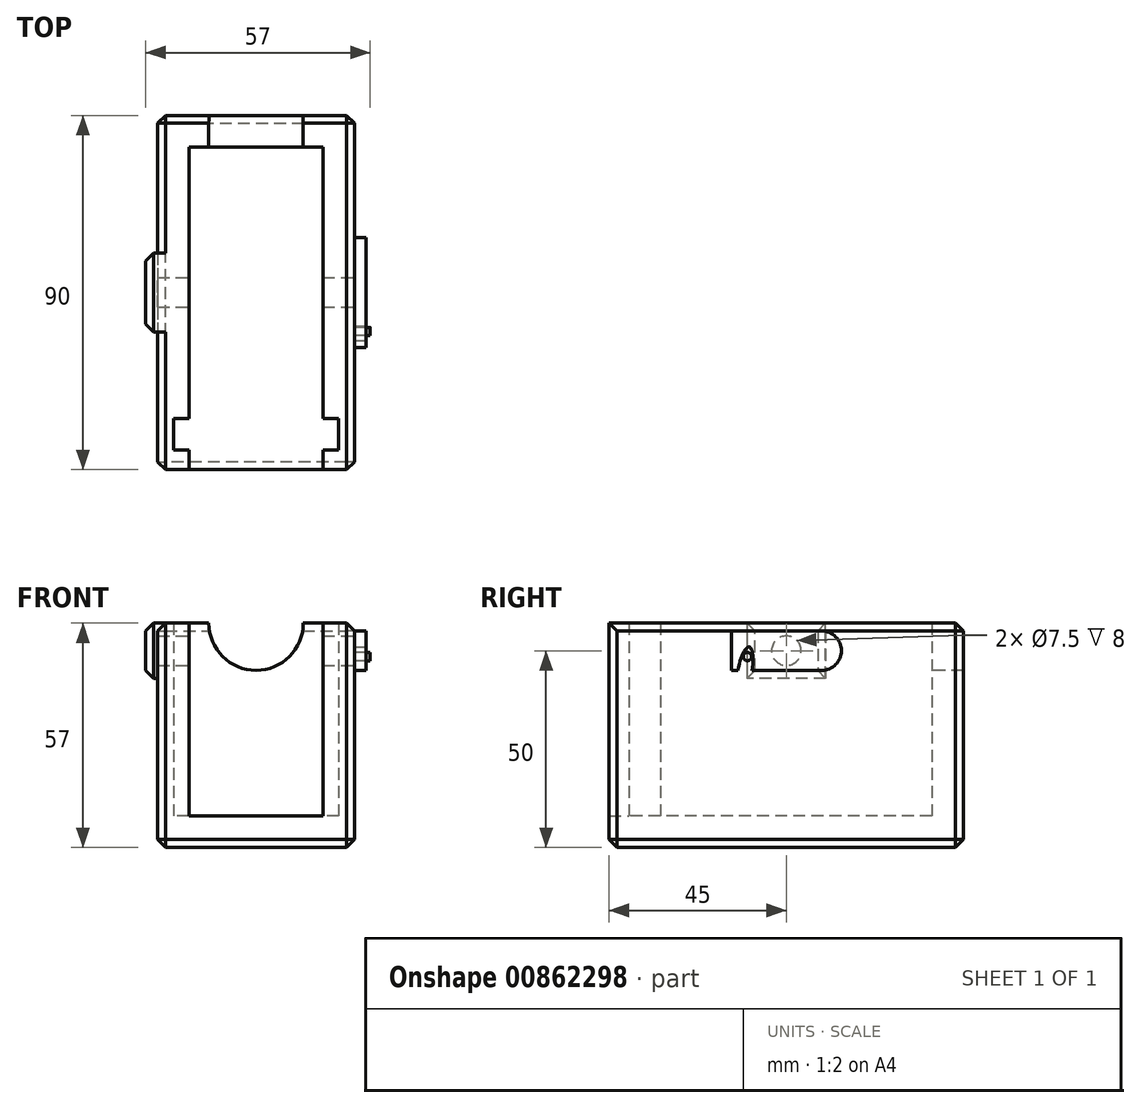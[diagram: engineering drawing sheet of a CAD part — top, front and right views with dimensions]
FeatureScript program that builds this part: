
annotation { "Feature Type Name" : "Feature", "Feature Type Description" : "" }
export const myFeature = defineFeature(function(context is Context, id is Id, definition is map)
    precondition{}
    {
        {
            var Q0;
            Q0=qCreatedBy(makeId("Top.planeOp"),FACE);
            var sketch = newSketch(context, id + "F0", { "sketchPlane" : qUnion([Q0])});
            skLineSegment(sketch, "E0.bottom", {"start": v(25, 45) * mm, "end": v(-25, 45) * mm});
            skLineSegment(sketch, "E0.top", {"start": v(25, -45) * mm, "end": v(-25, -45) * mm});
            skLineSegment(sketch, "E0.left", {"start": v(25, 45) * mm, "end": v(25, -45) * mm});
            skLineSegment(sketch, "E0.right", {"start": v(-25, 45) * mm, "end": v(-25, -45) * mm});
            skPoint(sketch, "E0.middle", {"position": v(0, 0) * mm});
            skSolve(sketch);
        }
        {
            var Q0;
            Q0 = qSketchRegion(id + "F0", true);
            extrude(context, id + "F1", {"entities" : qUnion([Q0]), "depth" : -8 * mm, "offsetDistance" : 25 * mm});
        }
        {
            var Q0;
            Q0=qCreatedBy(makeId("Top.planeOp"),FACE);
            var sketch = newSketch(context, id + "F2", { "sketchPlane" : qUnion([Q0])});
            skLineSegment(sketch, "E1.bottom", {"start": v(-25, 45) * mm, "end": v(25, 45) * mm, "construction": true});
            skLineSegment(sketch, "E1.top", {"start": v(-25, -45) * mm, "end": v(25, -45) * mm, "construction": true});
            skLineSegment(sketch, "E1.left", {"start": v(-25, 45) * mm, "end": v(-25, -45) * mm, "construction": true});
            skLineSegment(sketch, "E1.right", {"start": v(25, 45) * mm, "end": v(25, -45) * mm, "construction": true});
            skPoint(sketch, "E1.middle", {"position": v(0, 0) * mm});
            skLineSegment(sketch, "E2.bottom", {"start": v(-25, 45) * mm, "end": v(25, 45) * mm});
            skLineSegment(sketch, "E2.left", {"start": v(-25, 45) * mm, "end": v(-25, 37) * mm});
            skLineSegment(sketch, "E2.right", {"start": v(25, 45) * mm, "end": v(25, 37) * mm});
            skLineSegment(sketch, "E3.bottom", {"start": v(-25, 45) * mm, "end": v(-17, 45) * mm});
            skLineSegment(sketch, "E3.top", {"start": v(-25, -45) * mm, "end": v(-17, -45) * mm});
            skLineSegment(sketch, "E3.left", {"start": v(-25, 45) * mm, "end": v(-25, -45) * mm});
            skLineSegment(sketch, "E4", {"start": v(17, 37) * mm, "end": v(-17, 37) * mm});
            skLineSegment(sketch, "E5.bottom", {"start": v(25, 45) * mm, "end": v(17, 45) * mm});
            skLineSegment(sketch, "E5.top", {"start": v(25, -45) * mm, "end": v(17, -45) * mm});
            skLineSegment(sketch, "E5.left", {"start": v(25, 45) * mm, "end": v(25, -45) * mm});
            skLineSegment(sketch, "E6", {"start": v(-17, 45) * mm, "end": v(-17, 37) * mm, "construction": true});
            skLineSegment(sketch, "E7", {"start": v(-25, 37) * mm, "end": v(-17, 37) * mm, "construction": true});
            skLineSegment(sketch, "E8", {"start": v(17, 45) * mm, "end": v(17, 37) * mm, "construction": true});
            skLineSegment(sketch, "E9", {"start": v(17, 37) * mm, "end": v(25, 37) * mm, "construction": true});
            skLineSegment(sketch, "E10", {"start": v(-17, 37) * mm, "end": v(-17, -32) * mm});
            skLineSegment(sketch, "E11", {"start": v(17, 37) * mm, "end": v(17, -32) * mm});
            skLineSegment(sketch, "E12", {"start": v(17, -45) * mm, "end": v(17, -40) * mm});
            skLineSegment(sketch, "E13", {"start": v(-17, -45) * mm, "end": v(-17, -40) * mm});
            skLineSegment(sketch, "E14", {"start": v(-17, -32) * mm, "end": v(-21, -32) * mm});
            skLineSegment(sketch, "E15", {"start": v(-21, -32) * mm, "end": v(-21, -40) * mm});
            skLineSegment(sketch, "E16", {"start": v(-21, -40) * mm, "end": v(-17, -40) * mm});
            skLineSegment(sketch, "E17", {"start": v(17, -32) * mm, "end": v(21, -32) * mm});
            skLineSegment(sketch, "E18", {"start": v(21, -32) * mm, "end": v(21, -40) * mm});
            skLineSegment(sketch, "E19", {"start": v(21, -40) * mm, "end": v(17, -40) * mm});
            skSolve(sketch);
        }
        {
            var Q0;
            Q0 = qSketchRegion(id + "F2", true);
            extrude(context, id + "F3", {"entities" : qUnion([Q0]), "operationType" : NewBodyOperationType.ADD, "depth" : 49 * mm, "offsetDistance" : 25 * mm});
        }
        {
            var Q0;
            Q0=qCreatedBy(makeId("Right.planeOp"),FACE);
            var sketch = newSketch(context, id + "F4", { "sketchPlane" : qUnion([Q0])});
            skLineSegment(sketch, "E20", {"start": v(0, 0) * mm, "end": v(0, 42) * mm, "construction": true});
            skCircle(sketch, "E21", {"center": v(0, 42) * mm, "radius": 3.75 * mm});
            skSolve(sketch);
        }
        {
            var Q0;
            Q0 = qSketchRegion(id + "F4", true);
            extrude(context, id + "F5", {"entities" : qUnion([Q0]), "operationType" : NewBodyOperationType.REMOVE, "endBound" : BoundingType.SYMMETRIC, "oppositeDirection" : true, "depth" : 50 * mm, "offsetDistance" : 25 * mm});
        }
        {
            var Q0;
            Q0=qCreatedBy(makeId("Front.planeOp"),FACE);
            var sketch = newSketch(context, id + "F6", { "sketchPlane" : qUnion([Q0])});
            skLineSegment(sketch, "E22", {"start": v(0, 0) * mm, "end": v(0, 49) * mm, "construction": true});
            skArc(sketch, "E23", {"start": v(12, 49) * mm, "mid": v(0, 37) * mm, "end": v(-12, 49) * mm});
            skLineSegment(sketch, "E24", {"start": v(12, 49) * mm, "end": v(-12, 49) * mm});
            skSolve(sketch);
        }
        {
            var Q0;
            Q0 = qSketchRegion(id + "F6", true);
            extrude(context, id + "F7", {"entities" : qUnion([Q0]), "operationType" : NewBodyOperationType.REMOVE, "oppositeDirection" : true, "depth" : 50 * mm, "offsetDistance" : 25 * mm});
        }
        {
            var Q0;
            Q0=qCreatedBy(makeId("Right.planeOp"),FACE);
            var sketch = newSketch(context, id + "F8", { "sketchPlane" : qUnion([Q0])});
            skLineSegment(sketch, "E25", {"start": v(0, 0) * mm, "end": v(0, 42) * mm, "construction": true});
            skLineSegment(sketch, "E26.bottom", {"start": v(10, 49) * mm, "end": v(-10, 49) * mm});
            skLineSegment(sketch, "E26.top", {"start": v(10, 35) * mm, "end": v(-10, 35) * mm});
            skLineSegment(sketch, "E26.left", {"start": v(10, 49) * mm, "end": v(10, 35) * mm});
            skLineSegment(sketch, "E26.right", {"start": v(-10, 49) * mm, "end": v(-10, 35) * mm});
            skPoint(sketch, "E26.middle", {"position": v(0, 42) * mm});
            skSolve(sketch);
        }
        {
            var Q0;
            Q0 = qSketchRegion(id + "F8", true);
            extrude(context, id + "F9", {"entities" : qUnion([Q0]), "operationType" : NewBodyOperationType.ADD, "oppositeDirection" : true, "depth" : 28 * mm, "offsetDistance" : 25 * mm, "hasSecondDirection" : true, "secondDirectionOppositeDirection" : false, "secondDirectionDepth" : -25 * mm});
        }
        {
            var Q0;
            Q0=qCreatedBy(makeId("Right.planeOp"),FACE);
            var sketch = newSketch(context, id + "F10", { "sketchPlane" : qUnion([Q0])});
            skLineSegment(sketch, "E27", {"start": v(0, 0) * mm, "end": v(0, 42) * mm, "construction": true});
            skLineSegment(sketch, "E28.bottom", {"start": v(9, 47) * mm, "end": v(-14, 47) * mm});
            skLineSegment(sketch, "E28.top", {"start": v(9, 37) * mm, "end": v(-8.72, 37) * mm});
            skLineSegment(sketch, "E28.right", {"start": v(-14, 47) * mm, "end": v(-14, 37) * mm});
            skPoint(sketch, "E28.middle", {"position": v(0, 42) * mm});
            skLineSegment(sketch, "E29", {"start": v(-14, 37) * mm, "end": v(-12.27, 37) * mm, "construction": true});
            skArc(sketch, "E30", {"start": v(9, 37) * mm, "mid": v(12.54, 38.46) * mm, "end": v(14, 42) * mm});
            skLineSegment(sketch, "E31", {"start": v(9, 37) * mm, "end": v(9, 47) * mm, "construction": true});
            skArc(sketch, "E32", {"start": v(14, 42) * mm, "mid": v(12.54, 45.54) * mm, "end": v(9, 47) * mm});
            skPoint(sketch, "E33.orphan", {"position": v(14, 37) * mm});
            skPoint(sketch, "E34.orphan", {"position": v(14, 47) * mm});
            skEllipticalArc(sketch, "E35", {});
            skLineSegment(sketch, "E36", {"start": v(9, 37) * mm, "end": v(-8.72, 37) * mm, "construction": true});
            skLineSegment(sketch, "E37", {"start": v(-8.72, 37) * mm, "end": v(9, 37) * mm});
            skLineSegment(sketch, "E38", {"start": v(-12.27, 37) * mm, "end": v(-14, 37) * mm});
            skLineSegment(sketch, "E39.trimOffspring", {"start": v(-8.72, 37) * mm, "end": v(9, 37) * mm, "construction": true});
            skLineSegment(sketch, "E40.trimOffspring", {"start": v(-12.28, 37) * mm, "end": v(-14, 37) * mm});
            const initialGuessF10  = {"E35": [-0.010498499999999997, 0.037, 0.17990183921045588, 0.983684567454779, 0.006, 0.00175, 4.765680137042853, 1.6240874834530625]};
            skSetInitialGuess(sketch, initialGuessF10);
            skSolve(sketch);
        }
        {
            var Q0;
            Q0 = qSketchRegion(id + "F10", true);
            extrude(context, id + "F11", {"entities" : qUnion([Q0]), "operationType" : NewBodyOperationType.ADD, "depth" : 28 * mm, "offsetDistance" : 25 * mm, "hasSecondDirection" : true, "secondDirectionOppositeDirection" : true, "secondDirectionDepth" : -25 * mm});
        }
        {
            var Q0;
            Q0=qCreatedBy(makeId("Right.planeOp"),FACE);
            var sketch = newSketch(context, id + "F12", { "sketchPlane" : qUnion([Q0])});
            skCircle(sketch, "E41", {"center": v(-9.9, 40.5) * mm, "radius": 1.05 * mm});
            skSolve(sketch);
        }
        {
            var Q0;
            Q0 = qSketchRegion(id + "F12", true);
            extrude(context, id + "F13", {"entities" : qUnion([Q0]), "operationType" : NewBodyOperationType.ADD, "depth" : 29 * mm, "offsetDistance" : 25 * mm, "hasSecondDirection" : true, "secondDirectionOppositeDirection" : false, "secondDirectionDepth" : 25 * mm});
        }
        {
            var Q0;
            Q0=makeQuery(id+"F1.opExtrude","CAP_EDGE",EDGE,{"disambiguationData":[OSD([sQuery(id+"F0.wireOp",EDGE,"E0.left")])],"isStart":false});
            var Q1;
            Q1=makeQuery(id+"F3.boolean.opBoolean","MERGE",EDGE,{"derivedFrom":[makeQuery(id+"F1.opExtrude","SWEPT_EDGE",EDGE,{"disambiguationData":[OSD([sQuery(id+"F0.wireOp",EDGE,"E0.top"),sQuery(id+"F0.wireOp",EDGE,"E0.left")])]}),makeQuery(id+"F3.opExtrude","SWEPT_EDGE",EDGE,{"disambiguationData":[OSD([sQuery(id+"F2.wireOp",EDGE,"E5.top"),sQuery(id+"F2.wireOp",EDGE,"E5.left")])]})]});
            var Q2;
            Q2=makeQuery(id+"F1.opExtrude","CAP_EDGE",EDGE,{"disambiguationData":[OSD([sQuery(id+"F0.wireOp",EDGE,"E0.top")])],"isStart":false});
            var Q3;
            Q3=makeQuery(id+"F3.boolean.opBoolean","MERGE",EDGE,{"derivedFrom":[makeQuery(id+"F1.opExtrude","SWEPT_EDGE",EDGE,{"disambiguationData":[OSD([sQuery(id+"F0.wireOp",EDGE,"E0.top"),sQuery(id+"F0.wireOp",EDGE,"E0.right")])]}),makeQuery(id+"F3.opExtrude","SWEPT_EDGE",EDGE,{"disambiguationData":[OSD([sQuery(id+"F2.wireOp",EDGE,"E3.top"),sQuery(id+"F2.wireOp",EDGE,"E3.left")])]})]});
            var Q4;
            Q4=makeQuery(id+"F1.opExtrude","CAP_EDGE",EDGE,{"disambiguationData":[OSD([sQuery(id+"F0.wireOp",EDGE,"E0.right")])],"isStart":false});
            var Q5;
            Q5=makeQuery(id+"F3.boolean.opBoolean","MERGE",EDGE,{"derivedFrom":[makeQuery(id+"F1.opExtrude","SWEPT_EDGE",EDGE,{"disambiguationData":[OSD([sQuery(id+"F0.wireOp",EDGE,"E0.bottom"),sQuery(id+"F0.wireOp",EDGE,"E0.right")])]}),makeQuery(id+"F3.opExtrude","SWEPT_EDGE",EDGE,{"disambiguationData":[OSD([sQuery(id+"F2.wireOp",EDGE,"E3.bottom"),sQuery(id+"F2.wireOp",EDGE,"E3.left")])]})]});
            var Q6;
            Q6=makeQuery(id+"F3.boolean.opBoolean","MERGE",EDGE,{"derivedFrom":[makeQuery(id+"F1.opExtrude","SWEPT_EDGE",EDGE,{"disambiguationData":[OSD([sQuery(id+"F0.wireOp",EDGE,"E0.bottom"),sQuery(id+"F0.wireOp",EDGE,"E0.left")])]}),makeQuery(id+"F3.opExtrude","SWEPT_EDGE",EDGE,{"disambiguationData":[OSD([sQuery(id+"F2.wireOp",EDGE,"E5.bottom"),sQuery(id+"F2.wireOp",EDGE,"E5.left")])]})]});
            var Q7;
            Q7=makeQuery(id+"F1.opExtrude","CAP_EDGE",EDGE,{"disambiguationData":[OSD([sQuery(id+"F0.wireOp",EDGE,"E0.bottom")])],"isStart":false});
            var Q8;
            Q8=makeQuery(id+"F9.opExtrude","CAP_EDGE",EDGE,{"disambiguationData":[OSD([sQuery(id+"F8.wireOp",EDGE,"E26.bottom")])],"isStart":false});
            var Q9;
            {var subQ0=sQuery(id+"F2.wireOp",EDGE,"E5.bottom");var subQ2=sQuery(id+"F2.wireOp",EDGE,"E3.bottom");var subQ3=sQuery(id+"F2.wireOp",EDGE,"E2.bottom");Q9=makeQuery(id+"F7.boolean.opBoolean","SPLIT",EDGE,{"disambiguationData":[TD([makeQuery(id+"F1.opExtrude","SWEPT_FACE",FACE,{"disambiguationData":[OSD([sQuery(id+"F0.wireOp",EDGE,"E0.right")])]})])],"derivedFrom":makeQuery(id+"F3.opExtrude","CAP_EDGE",EDGE,{"disambiguationData":[OSD([subQ3,subQ2,subQ0])],"isStart":false})});}
            var Q10;
            {var subQ1=sQuery(id+"F2.wireOp",EDGE,"E5.bottom");var subQ2=sQuery(id+"F2.wireOp",EDGE,"E3.bottom");var subQ3=sQuery(id+"F2.wireOp",EDGE,"E2.bottom");Q10=makeQuery(id+"F7.boolean.opBoolean","SPLIT",EDGE,{"disambiguationData":[TD([makeQuery(id+"F1.opExtrude","SWEPT_FACE",FACE,{"disambiguationData":[OSD([sQuery(id+"F0.wireOp",EDGE,"E0.left")])]})])],"derivedFrom":makeQuery(id+"F3.opExtrude","CAP_EDGE",EDGE,{"disambiguationData":[OSD([subQ3,subQ2,subQ1])],"isStart":false})});}
            var Q11;
            Q11=makeQuery(id+"F3.opExtrude","CAP_EDGE",EDGE,{"disambiguationData":[OSD([sQuery(id+"F2.wireOp",EDGE,"E5.left")])],"isStart":false});
            var Q12;
            {var subQ1=sQuery(id+"F2.wireOp",EDGE,"E3.left");Q12=makeQuery(id+"F9.boolean.opBoolean","SPLIT",EDGE,{"disambiguationData":[TD([makeQuery(id+"F1.opExtrude","SWEPT_FACE",FACE,{"disambiguationData":[OSD([sQuery(id+"F0.wireOp",EDGE,"E0.bottom")])]})])],"derivedFrom":makeQuery(id+"F3.opExtrude","CAP_EDGE",EDGE,{"disambiguationData":[OSD([subQ1])],"isStart":false})});}
            var Q13;
            {var subQ2=sQuery(id+"F2.wireOp",EDGE,"E3.left");Q13=makeQuery(id+"F9.boolean.opBoolean","SPLIT",EDGE,{"disambiguationData":[TD([makeQuery(id+"F1.opExtrude","SWEPT_FACE",FACE,{"disambiguationData":[OSD([sQuery(id+"F0.wireOp",EDGE,"E0.top")])]})])],"derivedFrom":makeQuery(id+"F3.opExtrude","CAP_EDGE",EDGE,{"disambiguationData":[OSD([subQ2])],"isStart":false})});}
            var Q14;
            Q14=makeQuery(id+"F9.opExtrude","CAP_EDGE",EDGE,{"disambiguationData":[OSD([sQuery(id+"F8.wireOp",EDGE,"E26.left")])],"isStart":false});
            var Q15;
            Q15=makeQuery(id+"F9.opExtrude","CAP_EDGE",EDGE,{"disambiguationData":[OSD([sQuery(id+"F8.wireOp",EDGE,"E26.top")])],"isStart":false});
            var Q16;
            Q16=makeQuery(id+"F9.opExtrude","CAP_EDGE",EDGE,{"disambiguationData":[OSD([sQuery(id+"F8.wireOp",EDGE,"E26.right")])],"isStart":false});
            chamfer(context, id + "F14", {"entities" : qUnion([Q0, Q1, Q2, Q3, Q4, Q5, Q6, Q7, Q8, Q9, Q10, Q11, Q12, Q13, Q14, Q15, Q16]), "width" : 2 * mm, "tangentPropagation" : true});
        }
    });
